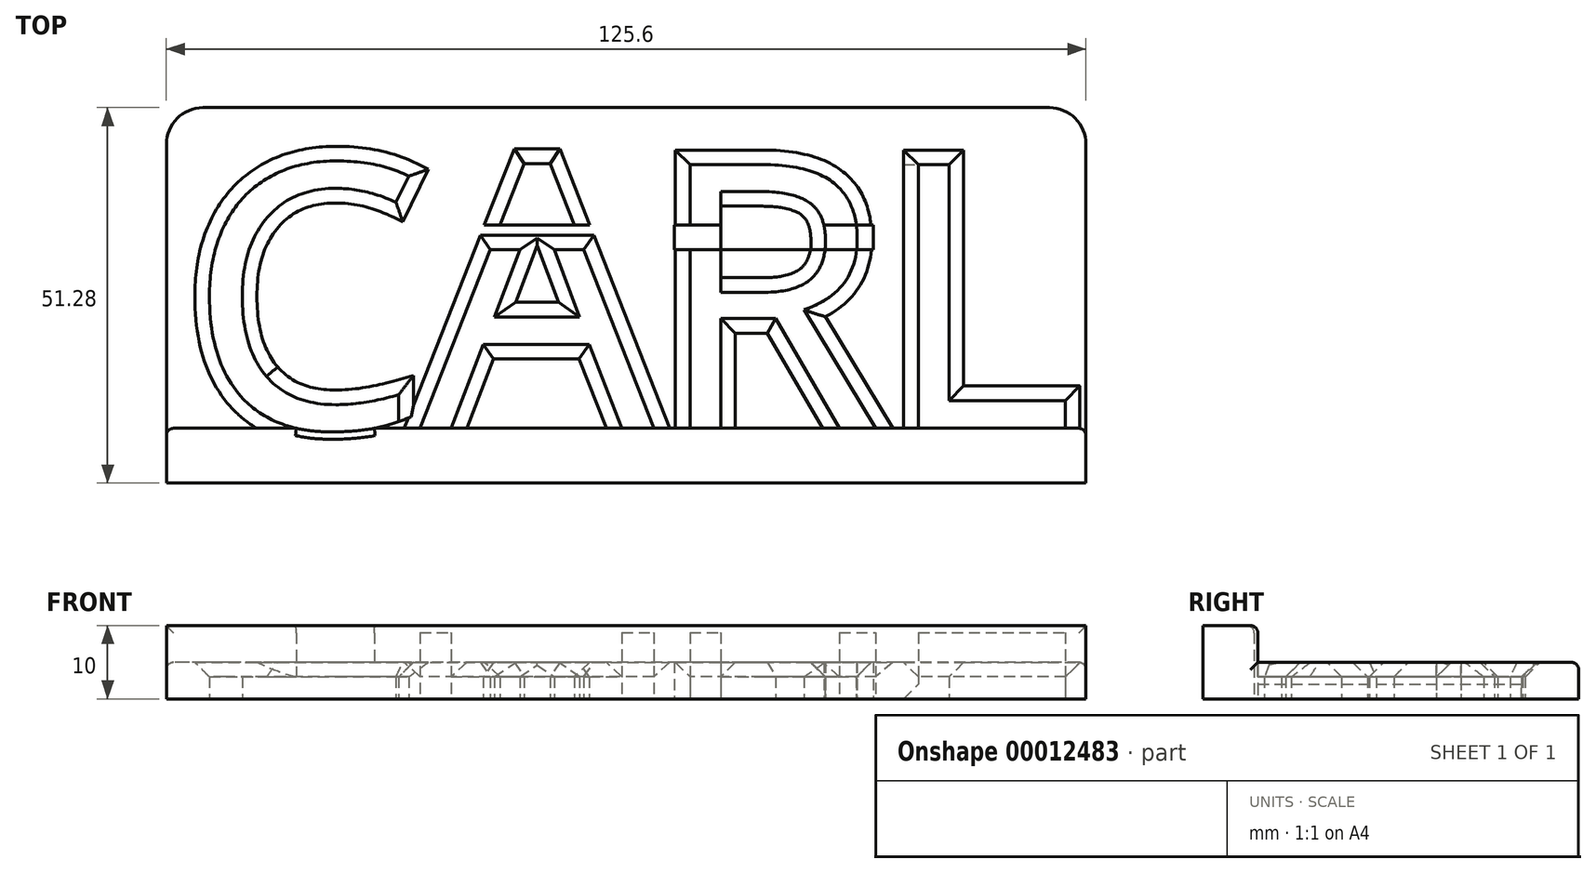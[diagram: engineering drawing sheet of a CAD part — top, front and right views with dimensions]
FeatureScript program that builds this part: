
annotation { "Feature Type Name" : "Feature", "Feature Type Description" : "" }
export const myFeature = defineFeature(function(context is Context, id is Id, definition is map)
    precondition{}
    {
        {
            var Q0;
            Q0=qCreatedBy(makeId("Top.planeOp"),FACE);
            var sketch = newSketch(context, id + "F0", { "sketchPlane" : qUnion([Q0])});
            skLineSegment(sketch, "E0.rect.bottom", {"start": v(60, -18.17) * mm, "end": v(-60, -18.17) * mm, "construction": true});
            skLineSegment(sketch, "E0.rect.top", {"start": v(60, 18.17) * mm, "end": v(-60, 18.17) * mm, "construction": true});
            skLineSegment(sketch, "E0.rect.left", {"start": v(60, -18.17) * mm, "end": v(60, 18.17) * mm, "construction": true});
            skLineSegment(sketch, "E0.rect.right", {"start": v(-60, -18.17) * mm, "end": v(-60, 18.17) * mm, "construction": true});
            skPoint(sketch, "E0.rect.middle", {"position": v(0, 0) * mm});
            skText(sketch, "E1", { "text": "CARL", "fontName": "OpenSans-Regular.ttf"});
            skLineSegment(sketch, "E2.rect.bottom", {"start": v(62.8, -25.64) * mm, "end": v(-62.8, -25.64) * mm});
            skLineSegment(sketch, "E2.rect.top", {"start": v(62.8, 25.64) * mm, "end": v(-62.8, 25.64) * mm});
            skLineSegment(sketch, "E2.rect.left", {"start": v(62.8, -25.64) * mm, "end": v(62.8, 25.64) * mm});
            skLineSegment(sketch, "E2.rect.right", {"start": v(-62.8, -25.64) * mm, "end": v(-62.8, 25.64) * mm});
            skLineSegment(sketch, "E3.top", {"start": v(62.8, -18.17) * mm, "end": v(-62.8, -18.17) * mm});
            skLineSegment(sketch, "E3.left", {"start": v(62.8, -25.64) * mm, "end": v(62.8, -18.17) * mm});
            skLineSegment(sketch, "E3.right", {"start": v(-62.8, -25.64) * mm, "end": v(-62.8, -18.17) * mm});
            skLineSegment(sketch, "E4.bottom", {"start": v(33.72, 9.6) * mm, "end": v(6.57, 9.6) * mm});
            skLineSegment(sketch, "E4.top", {"start": v(33.72, 6.21) * mm, "end": v(6.57, 6.21) * mm});
            skLineSegment(sketch, "E4.left", {"start": v(33.72, 9.6) * mm, "end": v(33.72, 6.21) * mm});
            skLineSegment(sketch, "E4.right", {"start": v(6.57, 9.6) * mm, "end": v(6.57, 6.21) * mm});
            skLineSegment(sketch, "E5.bottom", {"start": v(2.2, 9.6) * mm, "end": v(-23.2, 9.6) * mm});
            skLineSegment(sketch, "E5.top", {"start": v(2.2, 6.21) * mm, "end": v(-23.2, 6.21) * mm});
            skLineSegment(sketch, "E5.left", {"start": v(2.2, 9.6) * mm, "end": v(2.2, 6.21) * mm});
            skLineSegment(sketch, "E5.right", {"start": v(-23.2, 9.6) * mm, "end": v(-23.2, 6.21) * mm});
            const initialGuessF0  = {"E1": [-0.06, -0.01817, 1, 0, 0.03633]};
            skSetInitialGuess(sketch, initialGuessF0);
            skSolve(sketch);
        }
        {
            var Q0;
            Q0=makeQuery(id+"F0.imprint","IMPRINT",FACE,{"disambiguationData":[TD([[makeQuery(id+"F0.imprint","IMPRINT",EDGE,{"derivedFrom":sQuery(id+"F0.wireOp",EDGE,"E1.sketch_text.stroke-0")}),1.0]])]});
            var Q1;
            Q1=makeQuery(id+"F0.imprint","IMPRINT",FACE,{"disambiguationData":[TD([[makeQuery(id+"F0.imprint","IMPRINT",EDGE,{"derivedFrom":sQuery(id+"F0.wireOp",EDGE,"E1.sketch_text.stroke-23")}),1.0]])]});
            var Q2;
            Q2=makeQuery(id+"F0.imprint","IMPRINT",FACE,{"disambiguationData":[TD([[makeQuery(id+"F0.imprint","IMPRINT",EDGE,{"derivedFrom":sQuery(id+"F0.wireOp",EDGE,"E1.sketch_text.stroke-39")}),1.0]])]});
            extrude(context, id + "F1", {"entities" : qUnion([Q0, Q1, Q2]), "depth" : 5 * mm});
        }
        {
            var Q0;
            Q0=makeQuery(id+"F0.imprint","IMPRINT",FACE,{"disambiguationData":[TD([[makeQuery(id+"F0.imprint","IMPRINT",EDGE,{"derivedFrom":sQuery(id+"F0.wireOp",EDGE,"E2.rect.bottom")}),-1.0]])]});
            extrude(context, id + "F2", {"entities" : qUnion([Q0]), "operationType" : NewBodyOperationType.ADD, "depth" : 10 * mm});
        }
        {
            var Q0;
            {var subQ3=sQuery(id+"F0.wireOp",EDGE,"E1.sketch_text.stroke-34");var subQ9=sQuery(id+"F0.wireOp",EDGE,"E1.sketch_text.stroke-33");var subQ11=makeQuery(id+"F0.imprint","INTERSECT",VERTEX,{"derivedFrom":[subQ9,subQ3]});Q0=makeQuery(id+"F0.imprint","IMPRINT",FACE,{"disambiguationData":[TD([[makeQuery(id+"F0.imprint","IMPRINT",EDGE,{"disambiguationData":[TD([[subQ11,1.0]])],"derivedFrom":subQ9}),-1.0]])]});}
            extrude(context, id + "F3", {"entities" : qUnion([Q0]), "depth" : 5 * mm});
        }
        {
            var Q0;
            {var subQ3=sQuery(id+"F0.wireOp",EDGE,"E1.sketch_text.stroke-41");var subQ7=sQuery(id+"F0.wireOp",EDGE,"E1.sketch_text.stroke-42");var subQ9=makeQuery(id+"F0.imprint","INTERSECT",VERTEX,{"derivedFrom":[subQ3,subQ7]});Q0=makeQuery(id+"F0.imprint","IMPRINT",FACE,{"disambiguationData":[TD([[makeQuery(id+"F0.imprint","IMPRINT",EDGE,{"disambiguationData":[TD([[subQ9,1.0]])],"derivedFrom":subQ3}),1.0]])]});}
            var Q1;
            {var subQ6=sQuery(id+"F0.wireOp",EDGE,"E1.sketch_text.stroke-43");Q1=makeQuery(id+"F0.imprint","IMPRINT",FACE,{"disambiguationData":[TD([[makeQuery(id+"F0.imprint","IMPRINT",EDGE,{"derivedFrom":subQ6}),1.0]])]});}
            extrude(context, id + "F4", {"entities" : qUnion([Q0, Q1]), "depth" : 5 * mm});
        }
        {
            var Q0;
            {var subQ0=sQuery(id+"F0.wireOp",EDGE,"E4.left");Q0=makeQuery(id+"F0.imprint","IMPRINT",FACE,{"disambiguationData":[TD([[makeQuery(id+"F0.imprint","IMPRINT",EDGE,{"derivedFrom":subQ0}),-1.0]])]});}
            extrude(context, id + "F5", {"entities" : qUnion([Q0]), "depth" : 5 * mm});
        }
        {
            var Q0;
            {var subQ3=sQuery(id+"F0.wireOp",EDGE,"E1.sketch_text.stroke-30");var subQ5=sQuery(id+"F0.wireOp",EDGE,"E4.top");var subQ7=makeQuery(id+"F0.imprint","INTERSECT",VERTEX,{"derivedFrom":[subQ3,subQ5]});Q0=makeQuery(id+"F0.imprint","IMPRINT",FACE,{"disambiguationData":[TD([[makeQuery(id+"F0.imprint","IMPRINT",EDGE,{"disambiguationData":[TD([[subQ7,-1.0]])],"derivedFrom":subQ3}),-1.0]])]});}
            var Q1;
            {var subQ3=sQuery(id+"F0.wireOp",EDGE,"E4.right");Q1=makeQuery(id+"F0.imprint","IMPRINT",FACE,{"disambiguationData":[TD([[makeQuery(id+"F0.imprint","IMPRINT",EDGE,{"derivedFrom":subQ3}),1.0]])]});}
            extrude(context, id + "F6", {"entities" : qUnion([Q0, Q1]), "depth" : 5 * mm});
        }
        {
            var Q0;
            {var subQ2=sQuery(id+"F0.wireOp",EDGE,"E1.sketch_text.stroke-28");Q0=makeQuery(id+"F0.imprint","IMPRINT",FACE,{"disambiguationData":[TD([[makeQuery(id+"F0.imprint","IMPRINT",EDGE,{"derivedFrom":subQ2}),1.0]])]});}
            var Q1;
            {var subQ2=sQuery(id+"F0.wireOp",EDGE,"E1.sketch_text.stroke-15");Q1=makeQuery(id+"F0.imprint","IMPRINT",FACE,{"disambiguationData":[TD([[makeQuery(id+"F0.imprint","IMPRINT",EDGE,{"derivedFrom":subQ2}),1.0]])]});}
            extrude(context, id + "F7", {"entities" : qUnion([Q0, Q1]), "operationType" : NewBodyOperationType.ADD, "depth" : 5 * mm});
        }
        {
            var Q0;
            {var subQ3=sQuery(id+"F0.wireOp",EDGE,"E5.right");Q0=makeQuery(id+"F0.imprint","IMPRINT",FACE,{"disambiguationData":[TD([[makeQuery(id+"F0.imprint","IMPRINT",EDGE,{"derivedFrom":subQ3}),1.0]])]});}
            var Q1;
            {var subQ0=sQuery(id+"F0.wireOp",EDGE,"E5.top");var subQ3=sQuery(id+"F0.wireOp",EDGE,"E1.sketch_text.stroke-19");var subQ4=makeQuery(id+"F0.imprint","INTERSECT",VERTEX,{"derivedFrom":[subQ3,subQ0]});Q1=makeQuery(id+"F0.imprint","IMPRINT",FACE,{"disambiguationData":[TD([[makeQuery(id+"F0.imprint","IMPRINT",EDGE,{"disambiguationData":[TD([[subQ4,-1.0]])],"derivedFrom":subQ3}),-1.0]])]});}
            var Q2;
            {var subQ3=sQuery(id+"F0.wireOp",EDGE,"E1.sketch_text.stroke-23");var subQ8=sQuery(id+"F0.wireOp",EDGE,"E1.sketch_text.stroke-24");var subQ11=makeQuery(id+"F0.imprint","INTERSECT",VERTEX,{"derivedFrom":[subQ3,subQ8]});Q2=makeQuery(id+"F0.imprint","IMPRINT",FACE,{"disambiguationData":[TD([[makeQuery(id+"F0.imprint","IMPRINT",EDGE,{"disambiguationData":[TD([[subQ11,1.0]])],"derivedFrom":subQ3}),1.0]])]});}
            var Q3;
            {var subQ3=sQuery(id+"F0.wireOp",EDGE,"E1.sketch_text.stroke-21");var subQ5=sQuery(id+"F0.wireOp",EDGE,"E5.bottom");var subQ8=makeQuery(id+"F0.imprint","INTERSECT",VERTEX,{"derivedFrom":[subQ3,subQ5]});Q3=makeQuery(id+"F0.imprint","IMPRINT",FACE,{"disambiguationData":[TD([[makeQuery(id+"F0.imprint","IMPRINT",EDGE,{"disambiguationData":[TD([[subQ8,-1.0]])],"derivedFrom":subQ3}),-1.0]])]});}
            var Q4;
            {var subQ0=sQuery(id+"F0.wireOp",EDGE,"E5.left");Q4=makeQuery(id+"F0.imprint","IMPRINT",FACE,{"disambiguationData":[TD([[makeQuery(id+"F0.imprint","IMPRINT",EDGE,{"derivedFrom":subQ0}),-1.0]])]});}
            extrude(context, id + "F8", {"entities" : qUnion([Q0, Q1, Q2, Q3, Q4]), "depth" : 5 * mm});
        }
        {
            var Q0;
            Q0=makeQuery(id+"F1.opExtrude","SWEPT_BODY",BODY,{"disambiguationData":[OSD([sQuery(id+"F0.wireOp",EDGE,"E1.sketch_text.stroke-0"),sQuery(id+"F0.wireOp",EDGE,"E1.sketch_text.stroke-1"),sQuery(id+"F0.wireOp",EDGE,"E1.sketch_text.stroke-2"),sQuery(id+"F0.wireOp",EDGE,"E1.sketch_text.stroke-3"),sQuery(id+"F0.wireOp",EDGE,"E1.sketch_text.stroke-4"),sQuery(id+"F0.wireOp",EDGE,"E1.sketch_text.stroke-5"),sQuery(id+"F0.wireOp",EDGE,"E1.sketch_text.stroke-6"),sQuery(id+"F0.wireOp",EDGE,"E1.sketch_text.stroke-7"),sQuery(id+"F0.wireOp",EDGE,"E1.sketch_text.stroke-8"),sQuery(id+"F0.wireOp",EDGE,"E1.sketch_text.stroke-9"),sQuery(id+"F0.wireOp",EDGE,"E1.sketch_text.stroke-10"),sQuery(id+"F0.wireOp",EDGE,"E1.sketch_text.stroke-11"),sQuery(id+"F0.wireOp",EDGE,"E1.sketch_text.stroke-12"),sQuery(id+"F0.wireOp",EDGE,"E1.sketch_text.stroke-13"),sQuery(id+"F0.wireOp",EDGE,"E1.sketch_text.stroke-14"),sQuery(id+"F0.wireOp",EDGE,"E1.sketch_text.stroke-19"),sQuery(id+"F0.wireOp",EDGE,"E1.sketch_text.stroke-20"),sQuery(id+"F0.wireOp",EDGE,"E1.sketch_text.stroke-21"),sQuery(id+"F0.wireOp",EDGE,"E1.sketch_text.stroke-30"),sQuery(id+"F0.wireOp",EDGE,"E1.sketch_text.stroke-31"),sQuery(id+"F0.wireOp",EDGE,"E1.sketch_text.stroke-32"),sQuery(id+"F0.wireOp",EDGE,"E1.sketch_text.stroke-33"),sQuery(id+"F0.wireOp",EDGE,"E1.sketch_text.stroke-34"),sQuery(id+"F0.wireOp",EDGE,"E1.sketch_text.stroke-35"),sQuery(id+"F0.wireOp",EDGE,"E1.sketch_text.stroke-46"),sQuery(id+"F0.wireOp",EDGE,"E1.sketch_text.stroke-47"),sQuery(id+"F0.wireOp",EDGE,"E1.sketch_text.stroke-48"),sQuery(id+"F0.wireOp",EDGE,"E1.sketch_text.stroke-49"),sQuery(id+"F0.wireOp",EDGE,"E1.sketch_text.stroke-50"),sQuery(id+"F0.wireOp",EDGE,"E2.rect.top"),sQuery(id+"F0.wireOp",EDGE,"E2.rect.left"),sQuery(id+"F0.wireOp",EDGE,"E2.rect.right"),sQuery(id+"F0.wireOp",EDGE,"E3.top"),sQuery(id+"F0.wireOp",EDGE,"E4.bottom"),sQuery(id+"F0.wireOp",EDGE,"E4.top"),sQuery(id+"F0.wireOp",EDGE,"E4.left"),sQuery(id+"F0.wireOp",EDGE,"E4.right"),sQuery(id+"F0.wireOp",EDGE,"E5.bottom"),sQuery(id+"F0.wireOp",EDGE,"E5.top"),sQuery(id+"F0.wireOp",EDGE,"E5.left"),sQuery(id+"F0.wireOp",EDGE,"E5.right")])]});
            var Q1;
            Q1=makeQuery(id+"F1.opExtrude","SWEPT_BODY",BODY,{"disambiguationData":[OSD([sQuery(id+"F0.wireOp",EDGE,"E1.sketch_text.stroke-23"),sQuery(id+"F0.wireOp",EDGE,"E1.sketch_text.stroke-26"),sQuery(id+"F0.wireOp",EDGE,"E1.sketch_text.stroke-27"),sQuery(id+"F0.wireOp",EDGE,"E5.top")])]});
            var Q2;
            Q2=makeQuery(id+"F8.opExtrude","SWEPT_BODY",BODY,{"disambiguationData":[OSD([sQuery(id+"F0.wireOp",EDGE,"E5.bottom"),sQuery(id+"F0.wireOp",EDGE,"E5.top"),sQuery(id+"F0.wireOp",EDGE,"E5.left"),sQuery(id+"F0.wireOp",EDGE,"E5.right")])]});
            booleanBodies(context, id + "F9", {"operationType" : BooleanOperationType.UNION, "tools" : qUnion([Q0, Q1, Q2])});
        }
        {
            var Q0;
            Q0=makeQuery(id+"F1.opExtrude","CAP_EDGE",EDGE,{"disambiguationData":[OSD([sQuery(id+"F0.wireOp",EDGE,"E2.rect.left")])],"isStart":false});
            var Q1;
            Q1=makeQuery(id+"F1.opExtrude","CAP_EDGE",EDGE,{"disambiguationData":[OSD([sQuery(id+"F0.wireOp",EDGE,"E2.rect.top")])],"isStart":false});
            var Q2;
            {var subQ0=sQuery(id+"F0.wireOp",EDGE,"E3.top");var subQ1=makeQuery(id+"F0.imprint","INTERSECT",VERTEX,{"derivedFrom":[sQuery(id+"F0.wireOp",EDGE,"E1.sketch_text.stroke-50"),subQ0]});var subQ2=makeQuery(id+"F0.imprint","INTERSECT",VERTEX,{"derivedFrom":[sQuery(id+"F0.wireOp",EDGE,"E1.sketch_text.stroke-46"),subQ0]});var subQ3=makeQuery(id+"F0.imprint","INTERSECT",VERTEX,{"derivedFrom":[sQuery(id+"F0.wireOp",EDGE,"E1.sketch_text.stroke-35"),subQ0]});var subQ5=makeQuery(id+"F0.imprint","INTERSECT",VERTEX,{"derivedFrom":[sQuery(id+"F0.wireOp",EDGE,"E1.sketch_text.stroke-28"),subQ0]});var subQ7=makeQuery(id+"F0.imprint","INTERSECT",VERTEX,{"derivedFrom":[sQuery(id+"F0.wireOp",EDGE,"E1.sketch_text.stroke-21"),subQ0]});var subQ8=makeQuery(id+"F0.imprint","INTERSECT",VERTEX,{"derivedFrom":[sQuery(id+"F0.wireOp",EDGE,"E1.sketch_text.stroke-15"),subQ0]});var subQ9=makeQuery(id+"F0.imprint","INTERSECT",VERTEX,{"derivedFrom":[sQuery(id+"F0.wireOp",EDGE,"E1.sketch_text.stroke-17"),subQ0]});var subQ10=makeQuery(id+"F0.imprint","INTERSECT",VERTEX,{"derivedFrom":[sQuery(id+"F0.wireOp",EDGE,"E1.sketch_text.stroke-19"),subQ0]});Q2=makeQuery(id+"F2.opExtrude","CAP_EDGE",EDGE,{"disambiguationData":[OSD([subQ0]),TDD([makeQuery(id+"F0.imprint","IMPRINT",EDGE,{"disambiguationData":[TD([[subQ1,1.0]])],"derivedFrom":subQ0}),makeQuery(id+"F0.imprint","IMPRINT",EDGE,{"disambiguationData":[TD([[subQ2,1.0]])],"derivedFrom":subQ0}),makeQuery(id+"F0.imprint","IMPRINT",EDGE,{"disambiguationData":[TD([[subQ3,1.0]])],"derivedFrom":subQ0}),makeQuery(id+"F0.imprint","IMPRINT",EDGE,{"disambiguationData":[TD([[subQ3,-1.0]])],"derivedFrom":subQ0}),makeQuery(id+"F0.imprint","IMPRINT",EDGE,{"disambiguationData":[TD([[subQ5,1.0]])],"derivedFrom":subQ0}),makeQuery(id+"F0.imprint","IMPRINT",EDGE,{"disambiguationData":[TD([[subQ5,-1.0]])],"derivedFrom":subQ0}),makeQuery(id+"F0.imprint","IMPRINT",EDGE,{"disambiguationData":[TD([[subQ7,1.0]])],"derivedFrom":subQ0}),makeQuery(id+"F0.imprint","IMPRINT",EDGE,{"disambiguationData":[TD([[subQ8,1.0]])],"derivedFrom":subQ0}),makeQuery(id+"F0.imprint","IMPRINT",EDGE,{"disambiguationData":[TD([[subQ8,-1.0]])],"derivedFrom":subQ0}),makeQuery(id+"F0.imprint","IMPRINT",EDGE,{"disambiguationData":[TD([[subQ9,-1.0]])],"derivedFrom":subQ0}),makeQuery(id+"F0.imprint","IMPRINT",EDGE,{"disambiguationData":[TD([[subQ10,-1.0]])],"derivedFrom":subQ0})])],"isStart":false});}
            var Q3;
            Q3=makeQuery(id+"F2.opExtrude","CAP_EDGE",EDGE,{"disambiguationData":[OSD([sQuery(id+"F0.wireOp",EDGE,"E1.sketch_text.stroke-7")])],"isStart":false});
            var Q4;
            {var subQ0=sQuery(id+"F0.wireOp",EDGE,"E3.top");Q4=makeQuery(id+"F2.opExtrude","CAP_EDGE",EDGE,{"disambiguationData":[OSD([subQ0]),TDD([makeQuery(id+"F0.imprint","IMPRINT",EDGE,{"disambiguationData":[TD([[makeQuery(id+"F0.imprint","INTERSECT",VERTEX,{"derivedFrom":[sQuery(id+"F0.wireOp",EDGE,"E1.sketch_text.stroke-7"),subQ0]}),-1.0]])],"derivedFrom":subQ0})])],"isStart":false});}
            var Q5;
            Q5=makeQuery(id+"F2.opExtrude","SWEPT_EDGE",EDGE,{"disambiguationData":[OSD([sQuery(id+"F0.wireOp",EDGE,"E2.rect.left"),sQuery(id+"F0.wireOp",EDGE,"E3.top"),sQuery(id+"F0.wireOp",EDGE,"E3.left")])]});
            var Q6;
            Q6=makeQuery(id+"F2.opExtrude","SWEPT_EDGE",EDGE,{"disambiguationData":[OSD([sQuery(id+"F0.wireOp",EDGE,"E2.rect.right"),sQuery(id+"F0.wireOp",EDGE,"E3.top"),sQuery(id+"F0.wireOp",EDGE,"E3.right")])]});
            var Q7;
            Q7=makeQuery(id+"F1.opExtrude","CAP_EDGE",EDGE,{"disambiguationData":[OSD([sQuery(id+"F0.wireOp",EDGE,"E2.rect.right")])],"isStart":false});
            fillet(context, id + "F10", {"entities" : qUnion([Q0, Q1, Q2, Q3, Q4, Q5, Q6, Q7]), "radius" : 1 * mm, "tangentPropagation" : true, "allowEdgeOverflow" : false});
        }
        {
            var Q0;
            Q0=makeQuery(id+"F1.opExtrude","SWEPT_EDGE",EDGE,{"disambiguationData":[OSD([sQuery(id+"F0.wireOp",EDGE,"E2.rect.top"),sQuery(id+"F0.wireOp",EDGE,"E2.rect.right")])]});
            var Q1;
            Q1=makeQuery(id+"F1.opExtrude","SWEPT_EDGE",EDGE,{"disambiguationData":[OSD([sQuery(id+"F0.wireOp",EDGE,"E2.rect.top"),sQuery(id+"F0.wireOp",EDGE,"E2.rect.left")])]});
            var Q2;
            Q2=makeQuery(id+"F2.opExtrude","CAP_EDGE",EDGE,{"disambiguationData":[OSD([sQuery(id+"F0.wireOp",EDGE,"E3.left")])],"isStart":false});
            var Q3;
            Q3=makeQuery(id+"F2.opExtrude","CAP_EDGE",EDGE,{"disambiguationData":[OSD([sQuery(id+"F0.wireOp",EDGE,"E3.right")])],"isStart":false});
            fillet(context, id + "F11", {"entities" : qUnion([Q0, Q1, Q2, Q3]), "radius" : 5 * mm, "tangentPropagation" : true, "allowEdgeOverflow" : false});
        }
        {
            var Q0;
            Q0=makeQuery(id+"F1.opExtrude","CAP_EDGE",EDGE,{"disambiguationData":[OSD([sQuery(id+"F0.wireOp",EDGE,"E1.sketch_text.stroke-9")])],"isStart":false});
            var Q1;
            Q1=makeQuery(id+"F1.opExtrude","CAP_EDGE",EDGE,{"disambiguationData":[OSD([sQuery(id+"F0.wireOp",EDGE,"E1.sketch_text.stroke-8")])],"isStart":false});
            var Q2;
            Q2=makeQuery(id+"F1.opExtrude","CAP_EDGE",EDGE,{"disambiguationData":[OSD([sQuery(id+"F0.wireOp",EDGE,"E1.sketch_text.stroke-7")])],"isStart":false});
            var Q3;
            Q3=makeQuery(id+"F1.opExtrude","CAP_EDGE",EDGE,{"disambiguationData":[OSD([sQuery(id+"F0.wireOp",EDGE,"E1.sketch_text.stroke-10")])],"isStart":false});
            var Q4;
            Q4=makeQuery(id+"F1.opExtrude","CAP_EDGE",EDGE,{"disambiguationData":[OSD([sQuery(id+"F0.wireOp",EDGE,"E1.sketch_text.stroke-11")])],"isStart":false});
            var Q5;
            Q5=makeQuery(id+"F1.opExtrude","CAP_EDGE",EDGE,{"disambiguationData":[OSD([sQuery(id+"F0.wireOp",EDGE,"E1.sketch_text.stroke-12")])],"isStart":false});
            var Q6;
            Q6=makeQuery(id+"F1.opExtrude","CAP_EDGE",EDGE,{"disambiguationData":[OSD([sQuery(id+"F0.wireOp",EDGE,"E1.sketch_text.stroke-13")])],"isStart":false});
            var Q7;
            Q7=makeQuery(id+"F1.opExtrude","CAP_EDGE",EDGE,{"disambiguationData":[OSD([sQuery(id+"F0.wireOp",EDGE,"E1.sketch_text.stroke-14")])],"isStart":false});
            var Q8;
            Q8=makeQuery(id+"F1.opExtrude","CAP_EDGE",EDGE,{"disambiguationData":[OSD([sQuery(id+"F0.wireOp",EDGE,"E1.sketch_text.stroke-0")])],"isStart":false});
            var Q9;
            Q9=makeQuery(id+"F1.opExtrude","CAP_EDGE",EDGE,{"disambiguationData":[OSD([sQuery(id+"F0.wireOp",EDGE,"E1.sketch_text.stroke-1")])],"isStart":false});
            var Q10;
            Q10=makeQuery(id+"F1.opExtrude","CAP_EDGE",EDGE,{"disambiguationData":[OSD([sQuery(id+"F0.wireOp",EDGE,"E1.sketch_text.stroke-2")])],"isStart":false});
            var Q11;
            Q11=makeQuery(id+"F1.opExtrude","CAP_EDGE",EDGE,{"disambiguationData":[OSD([sQuery(id+"F0.wireOp",EDGE,"E1.sketch_text.stroke-3")])],"isStart":false});
            var Q12;
            Q12=makeQuery(id+"F1.opExtrude","CAP_EDGE",EDGE,{"disambiguationData":[OSD([sQuery(id+"F0.wireOp",EDGE,"E1.sketch_text.stroke-4")])],"isStart":false});
            var Q13;
            Q13=makeQuery(id+"F1.opExtrude","CAP_EDGE",EDGE,{"disambiguationData":[OSD([sQuery(id+"F0.wireOp",EDGE,"E1.sketch_text.stroke-5")])],"isStart":false});
            var Q14;
            {var subQ0=sQuery(id+"F0.wireOp",EDGE,"E1.sketch_text.stroke-19");Q14=makeQuery(id+"F1.opExtrude","CAP_EDGE",EDGE,{"disambiguationData":[OSD([subQ0]),TDD([makeQuery(id+"F0.imprint","IMPRINT",EDGE,{"disambiguationData":[TD([[makeQuery(id+"F0.imprint","INTERSECT",VERTEX,{"derivedFrom":[subQ0,sQuery(id+"F0.wireOp",EDGE,"E3.top")]}),-1.0]])],"derivedFrom":subQ0})])],"isStart":false});}
            var Q15;
            {var subQ0=sQuery(id+"F0.wireOp",EDGE,"E5.top");var subQ9=sQuery(id+"F0.wireOp",EDGE,"E1.sketch_text.stroke-26");Q15=makeQuery(id+"F9.opBoolean","SPLIT",EDGE,{"disambiguationData":[TD([makeQuery(id+"F1.opExtrude","SWEPT_FACE",FACE,{"disambiguationData":[OSD([subQ9])]})])],"derivedFrom":makeQuery(id+"F8.opExtrude","CAP_EDGE",EDGE,{"disambiguationData":[OSD([subQ0])],"isStart":false})});}
            var Q16;
            Q16=makeQuery(id+"F1.opExtrude","CAP_EDGE",EDGE,{"disambiguationData":[OSD([sQuery(id+"F0.wireOp",EDGE,"E1.sketch_text.stroke-26")])],"isStart":false});
            var Q17;
            Q17=makeQuery(id+"F1.opExtrude","CAP_EDGE",EDGE,{"disambiguationData":[OSD([sQuery(id+"F0.wireOp",EDGE,"E1.sketch_text.stroke-27")])],"isStart":false});
            var Q18;
            Q18=makeQuery(id+"F1.opExtrude","CAP_EDGE",EDGE,{"disambiguationData":[OSD([sQuery(id+"F0.wireOp",EDGE,"E1.sketch_text.stroke-23")])],"isStart":false});
            var Q19;
            {var subQ0=sQuery(id+"F0.wireOp",EDGE,"E5.top");var subQ13=sQuery(id+"F0.wireOp",EDGE,"E1.sketch_text.stroke-23");Q19=makeQuery(id+"F9.opBoolean","SPLIT",EDGE,{"disambiguationData":[TD([makeQuery(id+"F1.opExtrude","SWEPT_FACE",FACE,{"disambiguationData":[OSD([subQ13])]})])],"derivedFrom":makeQuery(id+"F8.opExtrude","CAP_EDGE",EDGE,{"disambiguationData":[OSD([subQ0])],"isStart":false})});}
            var Q20;
            {var subQ0=sQuery(id+"F0.wireOp",EDGE,"E1.sketch_text.stroke-21");Q20=makeQuery(id+"F1.opExtrude","CAP_EDGE",EDGE,{"disambiguationData":[OSD([subQ0]),TDD([makeQuery(id+"F0.imprint","IMPRINT",EDGE,{"disambiguationData":[TD([[makeQuery(id+"F0.imprint","INTERSECT",VERTEX,{"derivedFrom":[subQ0,sQuery(id+"F0.wireOp",EDGE,"E3.top")]}),1.0]])],"derivedFrom":subQ0})])],"isStart":false});}
            var Q21;
            Q21=makeQuery(id+"F7.opExtrude","CAP_EDGE",EDGE,{"disambiguationData":[OSD([sQuery(id+"F0.wireOp",EDGE,"E1.sketch_text.stroke-15")])],"isStart":false});
            var Q22;
            Q22=makeQuery(id+"F7.opExtrude","CAP_EDGE",EDGE,{"disambiguationData":[OSD([sQuery(id+"F0.wireOp",EDGE,"E1.sketch_text.stroke-16")])],"isStart":false});
            var Q23;
            Q23=makeQuery(id+"F7.opExtrude","CAP_EDGE",EDGE,{"disambiguationData":[OSD([sQuery(id+"F0.wireOp",EDGE,"E1.sketch_text.stroke-17")])],"isStart":false});
            chamfer(context, id + "F12", {"entities" : qUnion([Q0, Q1, Q2, Q3, Q4, Q5, Q6, Q7, Q8, Q9, Q10, Q11, Q12, Q13, Q14, Q15, Q16, Q17, Q18, Q19, Q20, Q21, Q22, Q23]), "width" : 2 * mm});
        }
        {
            var Q0;
            {var subQ0=sQuery(id+"F0.wireOp",EDGE,"E1.sketch_text.stroke-19");Q0=makeQuery(id+"F1.opExtrude","CAP_EDGE",EDGE,{"disambiguationData":[OSD([subQ0]),TDD([makeQuery(id+"F0.imprint","IMPRINT",EDGE,{"disambiguationData":[TD([[makeQuery(id+"F0.imprint","INTERSECT",VERTEX,{"derivedFrom":[subQ0,sQuery(id+"F0.wireOp",EDGE,"E1.sketch_text.stroke-20")]}),1.0]])],"derivedFrom":subQ0})])],"isStart":false});}
            var Q1;
            Q1=makeQuery(id+"F1.opExtrude","CAP_EDGE",EDGE,{"disambiguationData":[OSD([sQuery(id+"F0.wireOp",EDGE,"E1.sketch_text.stroke-20")])],"isStart":false});
            var Q2;
            {var subQ0=sQuery(id+"F0.wireOp",EDGE,"E1.sketch_text.stroke-21");Q2=makeQuery(id+"F1.opExtrude","CAP_EDGE",EDGE,{"disambiguationData":[OSD([subQ0]),TDD([makeQuery(id+"F0.imprint","IMPRINT",EDGE,{"disambiguationData":[TD([[makeQuery(id+"F0.imprint","INTERSECT",VERTEX,{"derivedFrom":[sQuery(id+"F0.wireOp",EDGE,"E1.sketch_text.stroke-20"),subQ0]}),-1.0]])],"derivedFrom":subQ0})])],"isStart":false});}
            var Q3;
            {var subQ0=sQuery(id+"F0.wireOp",EDGE,"E1.sketch_text.stroke-30");Q3=makeQuery(id+"F1.opExtrude","CAP_EDGE",EDGE,{"disambiguationData":[OSD([subQ0]),TDD([makeQuery(id+"F0.imprint","IMPRINT",EDGE,{"disambiguationData":[TD([[makeQuery(id+"F0.imprint","INTERSECT",VERTEX,{"derivedFrom":[subQ0,sQuery(id+"F0.wireOp",EDGE,"E1.sketch_text.stroke-31")]}),1.0]])],"derivedFrom":subQ0})])],"isStart":false});}
            var Q4;
            {var subQ0=sQuery(id+"F0.wireOp",EDGE,"E1.sketch_text.stroke-30");Q4=makeQuery(id+"F1.opExtrude","CAP_EDGE",EDGE,{"disambiguationData":[OSD([subQ0]),TDD([makeQuery(id+"F0.imprint","IMPRINT",EDGE,{"disambiguationData":[TD([[makeQuery(id+"F0.imprint","INTERSECT",VERTEX,{"derivedFrom":[subQ0,sQuery(id+"F0.wireOp",EDGE,"E3.top")]}),-1.0]])],"derivedFrom":subQ0})])],"isStart":false});}
            var Q5;
            Q5=makeQuery(id+"F7.opExtrude","CAP_EDGE",EDGE,{"disambiguationData":[OSD([sQuery(id+"F0.wireOp",EDGE,"E1.sketch_text.stroke-28")])],"isStart":false});
            var Q6;
            Q6=makeQuery(id+"F7.opExtrude","CAP_EDGE",EDGE,{"disambiguationData":[OSD([sQuery(id+"F0.wireOp",EDGE,"E1.sketch_text.stroke-38")])],"isStart":false});
            var Q7;
            Q7=makeQuery(id+"F7.opExtrude","CAP_EDGE",EDGE,{"disambiguationData":[OSD([sQuery(id+"F0.wireOp",EDGE,"E1.sketch_text.stroke-37")])],"isStart":false});
            var Q8;
            Q8=makeQuery(id+"F1.opExtrude","CAP_EDGE",EDGE,{"disambiguationData":[OSD([sQuery(id+"F0.wireOp",EDGE,"E1.sketch_text.stroke-35")])],"isStart":false});
            var Q9;
            Q9=makeQuery(id+"F1.opExtrude","CAP_EDGE",EDGE,{"disambiguationData":[OSD([sQuery(id+"F0.wireOp",EDGE,"E1.sketch_text.stroke-39")])],"isStart":false});
            var Q10;
            Q10=makeQuery(id+"F1.opExtrude","CAP_EDGE",EDGE,{"disambiguationData":[OSD([sQuery(id+"F0.wireOp",EDGE,"E1.sketch_text.stroke-41")])],"isStart":false});
            var Q11;
            Q11=makeQuery(id+"F4.opExtrude","CAP_EDGE",EDGE,{"disambiguationData":[OSD([sQuery(id+"F0.wireOp",EDGE,"E1.sketch_text.stroke-42")])],"isStart":false});
            var Q12;
            Q12=makeQuery(id+"F4.opExtrude","CAP_EDGE",EDGE,{"disambiguationData":[OSD([sQuery(id+"F0.wireOp",EDGE,"E1.sketch_text.stroke-43")])],"isStart":false});
            var Q13;
            Q13=makeQuery(id+"F4.opExtrude","CAP_EDGE",EDGE,{"disambiguationData":[OSD([sQuery(id+"F0.wireOp",EDGE,"E1.sketch_text.stroke-44")])],"isStart":false});
            chamfer(context, id + "F13", {"entities" : qUnion([Q0, Q1, Q2, Q3, Q4, Q5, Q6, Q7, Q8, Q9, Q10, Q11, Q12, Q13]), "width" : 2 * mm});
        }
        {
            var Q0;
            Q0=makeQuery(id+"F1.opExtrude","CAP_EDGE",EDGE,{"disambiguationData":[OSD([sQuery(id+"F0.wireOp",EDGE,"E1.sketch_text.stroke-31")])],"isStart":false});
            var Q1;
            Q1=makeQuery(id+"F1.opExtrude","CAP_EDGE",EDGE,{"disambiguationData":[OSD([sQuery(id+"F0.wireOp",EDGE,"E1.sketch_text.stroke-34")])],"isStart":false});
            var Q2;
            Q2=makeQuery(id+"F1.opExtrude","CAP_EDGE",EDGE,{"disambiguationData":[OSD([sQuery(id+"F0.wireOp",EDGE,"E1.sketch_text.stroke-46")])],"isStart":true});
            var Q3;
            Q3=makeQuery(id+"F1.opExtrude","CAP_EDGE",EDGE,{"disambiguationData":[OSD([sQuery(id+"F0.wireOp",EDGE,"E1.sketch_text.stroke-48")])],"isStart":false});
            var Q4;
            Q4=makeQuery(id+"F1.opExtrude","CAP_EDGE",EDGE,{"disambiguationData":[OSD([sQuery(id+"F0.wireOp",EDGE,"E1.sketch_text.stroke-46")])],"isStart":false});
            var Q5;
            Q5=makeQuery(id+"F1.opExtrude","CAP_EDGE",EDGE,{"disambiguationData":[OSD([sQuery(id+"F0.wireOp",EDGE,"E1.sketch_text.stroke-47")])],"isStart":false});
            var Q6;
            Q6=makeQuery(id+"F1.opExtrude","CAP_EDGE",EDGE,{"disambiguationData":[OSD([sQuery(id+"F0.wireOp",EDGE,"E1.sketch_text.stroke-49")])],"isStart":false});
            chamfer(context, id + "F14", {"entities" : qUnion([Q0, Q1, Q2, Q3, Q4, Q5, Q6]), "width" : 2 * mm, "tangentPropagation" : true});
        }
        {
            var Q0;
            Q0=makeQuery(id+"F1.opExtrude","CAP_EDGE",EDGE,{"disambiguationData":[OSD([sQuery(id+"F0.wireOp",EDGE,"E1.sketch_text.stroke-50")])],"isStart":false});
            chamfer(context, id + "F15", {"entities" : qUnion([Q0]), "width" : 2 * mm, "tangentPropagation" : true});
        }
    });
